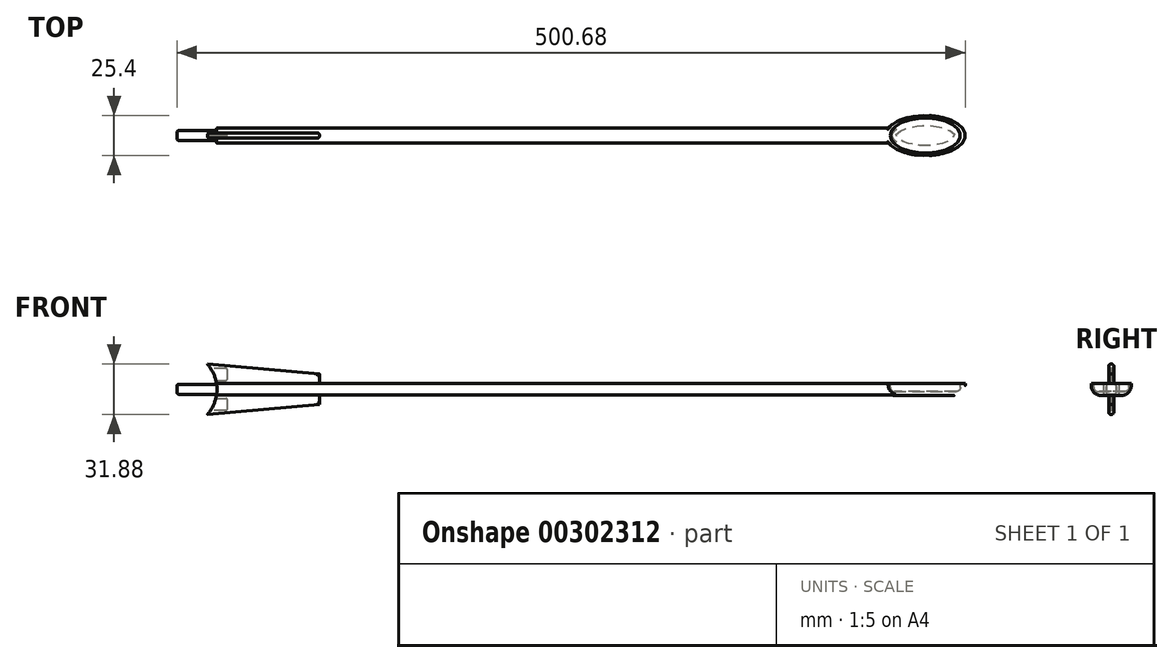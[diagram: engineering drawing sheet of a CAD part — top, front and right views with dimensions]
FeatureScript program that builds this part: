
annotation { "Feature Type Name" : "Feature", "Feature Type Description" : "" }
export const myFeature = defineFeature(function(context is Context, id is Id, definition is map)
    precondition{}
    {
        {
            var Q0;
            Q0=qCreatedBy(makeId("Top.planeOp"),FACE);
            var sketch = newSketch(context, id + "F0", { "sketchPlane" : qUnion([Q0])});
            skLineSegment(sketch, "E0.bottom", {"start": v(-215.55, -4.76) * mm, "end": v(215.55, -4.76) * mm});
            skLineSegment(sketch, "E0.top", {"start": v(-215.55, 4.76) * mm, "end": v(215.55, 4.76) * mm});
            skLineSegment(sketch, "E0.left", {"start": v(-215.55, -4.76) * mm, "end": v(-215.55, 4.76) * mm});
            skLineSegment(sketch, "E0.right", {"start": v(215.55, -4.76) * mm, "end": v(215.55, 4.76) * mm});
            skPoint(sketch, "E0.middle", {"position": v(0, 0) * mm});
            skSolve(sketch);
        }
        {
            var Q0;
            Q0 = qSketchRegion(id + "F0", true);
            extrude(context, id + "F1", {"entities" : qUnion([Q0]), "depth" : 7.24 * mm});
        }
        {
            var Q0;
            Q0=makeQuery(id+"F1.opExtrude","CAP_EDGE",EDGE,{"disambiguationData":[OSD([sQuery(id+"F0.wireOp",EDGE,"E0.bottom")])],"isStart":false});
            var Q1;
            Q1=makeQuery(id+"F1.opExtrude","CAP_EDGE",EDGE,{"disambiguationData":[OSD([sQuery(id+"F0.wireOp",EDGE,"E0.top")])],"isStart":false});
            var Q2;
            Q2=makeQuery(id+"F1.opExtrude","CAP_EDGE",EDGE,{"disambiguationData":[OSD([sQuery(id+"F0.wireOp",EDGE,"E0.bottom")])],"isStart":true});
            var Q3;
            Q3=makeQuery(id+"F1.opExtrude","CAP_EDGE",EDGE,{"disambiguationData":[OSD([sQuery(id+"F0.wireOp",EDGE,"E0.top")])],"isStart":true});
            fillet(context, id + "F2", {"entities" : qUnion([Q0, Q1, Q2, Q3]), "radius" : 1.27 * mm, "tangentPropagation" : true, "allowEdgeOverflow" : false});
        }
        {
            var Q0;
            Q0=makeQuery(id+"F1.opExtrude","CAP_FACE",FACE,{"disambiguationData":[OSD([sQuery(id+"F0.wireOp",EDGE,"E0.bottom"),sQuery(id+"F0.wireOp",EDGE,"E0.top"),sQuery(id+"F0.wireOp",EDGE,"E0.left"),sQuery(id+"F0.wireOp",EDGE,"E0.right")])],"isStart":false});
            var sketch = newSketch(context, id + "F3", { "sketchPlane" : qUnion([Q0])});
            skEllipse(sketch, "E1", {"center": v(234.6, 0) * mm, "majorRadius": 25.4 * mm, "minorRadius": 12.7 * mm, "majorAxis": v(-1, 0)});
            skPoint(sketch, "E1.centerSnap0", {"position": v(215.55, 0) * mm});
            skSolve(sketch);
        }
        {
            var Q0;
            Q0 = qSketchRegion(id + "F3", true);
            extrude(context, id + "F4", {"entities" : qUnion([Q0]), "operationType" : NewBodyOperationType.ADD, "oppositeDirection" : true, "depth" : 7.62 * mm});
        }
        {
            var Q0;
            Q0=makeQuery(id+"F4.opExtrude","CAP_EDGE",EDGE,{"disambiguationData":[OSD([sQuery(id+"F3.wireOp",EDGE,"E1")])],"isStart":false});
            fillet(context, id + "F5", {"entities" : qUnion([Q0]), "radius" : 6.35 * mm, "tangentPropagation" : true, "allowEdgeOverflow" : false});
        }
        {
            var Q0;
            Q0=makeQuery(id+"F4.boolean.opBoolean","MERGE",FACE,{"derivedFrom":[makeQuery(id+"F1.opExtrude","CAP_FACE",FACE,{"disambiguationData":[OSD([sQuery(id+"F0.wireOp",EDGE,"E0.bottom"),sQuery(id+"F0.wireOp",EDGE,"E0.top"),sQuery(id+"F0.wireOp",EDGE,"E0.left"),sQuery(id+"F0.wireOp",EDGE,"E0.right")])],"isStart":false}),makeQuery(id+"F4.opExtrude","CAP_FACE",FACE,{"disambiguationData":[OSD([sQuery(id+"F3.wireOp",EDGE,"E1")])],"isStart":true})]});
            var sketch = newSketch(context, id + "F6", { "sketchPlane" : qUnion([Q0])});
            skEllipse(sketch, "E2", {"center": v(234.6, 0) * mm, "majorRadius": 22.23 * mm, "minorRadius": 11.11 * mm, "majorAxis": v(-1, 0)});
            skSolve(sketch);
        }
        {
            var Q0;
            Q0 = qSketchRegion(id + "F6", true);
            extrude(context, id + "F7", {"entities" : qUnion([Q0]), "operationType" : NewBodyOperationType.REMOVE, "oppositeDirection" : true, "depth" : 5.08 * mm});
        }
        {
            var Q0;
            Q0=makeQuery(id+"F7.boolean.opBoolean","COPY",EDGE,{"derivedFrom":makeQuery(id+"F7.opExtrude","CAP_EDGE",EDGE,{"disambiguationData":[OSD([sQuery(id+"F6.wireOp",EDGE,"E2")])],"isStart":false})});
            fillet(context, id + "F8", {"entities" : qUnion([Q0]), "radius" : 2.54 * mm, "tangentPropagation" : true, "allowEdgeOverflow" : false});
        }
        {
            var Q0;
            Q0=makeQuery(id+"F1.opExtrude","SWEPT_FACE",FACE,{"disambiguationData":[OSD([sQuery(id+"F0.wireOp",EDGE,"E0.bottom")])]});
            var sketch = newSketch(context, id + "F9", { "sketchPlane" : qUnion([Q0])});
            skCircle(sketch, "E3", {"center": v(-239.09, 3.62) * mm, "radius": 23.81 * mm});
            skSolve(sketch);
        }
        {
            var Q0;
            Q0=qCreatedBy(makeId("Front.planeOp"),FACE);
            var sketch = newSketch(context, id + "F10", { "sketchPlane" : qUnion([Q0])});
            skLineSegment(sketch, "E4", {"start": v(-215.55, 7.24) * mm, "end": v(-228.5, 20.18) * mm});
            skLineSegment(sketch, "E5", {"start": v(-228.5, 20.18) * mm, "end": v(-150.2, 13.34) * mm});
            skLineSegment(sketch, "E6", {"start": v(-150.2, 13.34) * mm, "end": v(-150.2, 7.24) * mm});
            skLineSegment(sketch, "E7", {"start": v(-150.2, 7.24) * mm, "end": v(-215.55, 7.24) * mm});
            skLineSegment(sketch, "E8", {"start": v(-150.2, 0) * mm, "end": v(-150.2, -6.1) * mm});
            skLineSegment(sketch, "E9", {"start": v(-150.2, -6.1) * mm, "end": v(-228.5, -12.95) * mm});
            skLineSegment(sketch, "E10", {"start": v(-228.5, -12.95) * mm, "end": v(-215.55, 0) * mm});
            skLineSegment(sketch, "E11", {"start": v(-215.55, 0) * mm, "end": v(-150.2, 0) * mm});
            skSolve(sketch);
        }
        {
            var Q0;
            Q0=makeQuery(id+"F10.imprint","IMPRINT",FACE,{"disambiguationData":[TD([[makeQuery(id+"F10.imprint","IMPRINT",EDGE,{"derivedFrom":sQuery(id+"F10.wireOp",EDGE,"E4")}),-1.0]])]});
            var Q1;
            Q1=makeQuery(id+"F10.imprint","IMPRINT",FACE,{"disambiguationData":[TD([[makeQuery(id+"F10.imprint","IMPRINT",EDGE,{"derivedFrom":sQuery(id+"F10.wireOp",EDGE,"E8")}),-1.0]])]});
            var Q2;
            Q2 = qConstructionFilter(qBodyType(qCreatedBy(id + "F10" ,EDGE), BodyType.WIRE), ConstructionObject.NO);
            extrude(context, id + "F11", {"entities" : qUnion([Q0, Q1]), "operationType" : NewBodyOperationType.ADD, "surfaceEntities" : qUnion([Q2]), "endBound" : BoundingType.SYMMETRIC, "depth" : 3.17 * mm});
        }
        {
            var Q0;
            Q0 = qSketchRegion(id + "F9", true);
            extrude(context, id + "F12", {"entities" : qUnion([Q0]), "operationType" : NewBodyOperationType.REMOVE, "oppositeDirection" : true, "depth" : 25.4 * mm});
        }
        {
            var Q0;
            Q0=makeQuery(id+"F11.opExtrude","CAP_EDGE",EDGE,{"disambiguationData":[OSD([sQuery(id+"F10.wireOp",EDGE,"E5")])],"isStart":false});
            var Q1;
            Q1=makeQuery(id+"F11.opExtrude","CAP_EDGE",EDGE,{"disambiguationData":[OSD([sQuery(id+"F10.wireOp",EDGE,"E5")])],"isStart":true});
            var Q2;
            Q2=makeQuery(id+"F11.opExtrude","CAP_EDGE",EDGE,{"disambiguationData":[OSD([sQuery(id+"F10.wireOp",EDGE,"E7")])],"isStart":false});
            var Q3;
            Q3=makeQuery(id+"F11.opExtrude","SWEPT_EDGE",EDGE,{"disambiguationData":[OSD([sQuery(id+"F10.wireOp",EDGE,"E6"),sQuery(id+"F10.wireOp",EDGE,"E7")])]});
            var Q4;
            Q4=makeQuery(id+"F11.opExtrude","CAP_EDGE",EDGE,{"disambiguationData":[OSD([sQuery(id+"F10.wireOp",EDGE,"E6")])],"isStart":false});
            var Q5;
            Q5=makeQuery(id+"F11.opExtrude","CAP_EDGE",EDGE,{"disambiguationData":[OSD([sQuery(id+"F10.wireOp",EDGE,"E6")])],"isStart":true});
            var Q6;
            Q6=makeQuery(id+"F11.opExtrude","CAP_EDGE",EDGE,{"disambiguationData":[OSD([sQuery(id+"F10.wireOp",EDGE,"E7")])],"isStart":true});
            var Q7;
            Q7=makeQuery(id+"F11.opExtrude","CAP_EDGE",EDGE,{"disambiguationData":[OSD([sQuery(id+"F10.wireOp",EDGE,"E9")])],"isStart":true});
            var Q8;
            Q8=makeQuery(id+"F11.opExtrude","CAP_EDGE",EDGE,{"disambiguationData":[OSD([sQuery(id+"F10.wireOp",EDGE,"E8")])],"isStart":true});
            var Q9;
            Q9=makeQuery(id+"F11.opExtrude","CAP_EDGE",EDGE,{"disambiguationData":[OSD([sQuery(id+"F10.wireOp",EDGE,"E9")])],"isStart":false});
            var Q10;
            Q10=makeQuery(id+"F11.opExtrude","CAP_EDGE",EDGE,{"disambiguationData":[OSD([sQuery(id+"F10.wireOp",EDGE,"E8")])],"isStart":false});
            var Q11;
            Q11=makeQuery(id+"F11.opExtrude","CAP_EDGE",EDGE,{"disambiguationData":[OSD([sQuery(id+"F10.wireOp",EDGE,"E11")])],"isStart":false});
            var Q12;
            Q12=makeQuery(id+"F11.opExtrude","CAP_EDGE",EDGE,{"disambiguationData":[OSD([sQuery(id+"F10.wireOp",EDGE,"E11")])],"isStart":true});
            fillet(context, id + "F13", {"entities" : qUnion([Q0, Q1, Q2, Q3, Q4, Q5, Q6, Q7, Q8, Q9, Q10, Q11, Q12]), "radius" : 1.27 * mm, "tangentPropagation" : true, "allowEdgeOverflow" : false});
        }
        {
            var Q0;
            Q0=qCreatedBy(makeId("Right.planeOp"),FACE);
            var sketch = newSketch(context, id + "F14", { "sketchPlane" : qUnion([Q0])});
            skLineSegment(sketch, "E12.bottom", {"start": v(-3.17, 6.8) * mm, "end": v(3.18, 6.8) * mm});
            skLineSegment(sketch, "E12.top", {"start": v(-3.18, 0.44) * mm, "end": v(3.18, 0.44) * mm});
            skLineSegment(sketch, "E12.left", {"start": v(-3.17, 6.8) * mm, "end": v(-3.18, 0.44) * mm});
            skLineSegment(sketch, "E12.right", {"start": v(3.18, 6.8) * mm, "end": v(3.18, 0.44) * mm});
            skPoint(sketch, "E12.middle", {"position": v(0, 3.62) * mm});
            skSolve(sketch);
        }
        {
            var Q0;
            Q0 = qSketchRegion(id + "F14", true);
            extrude(context, id + "F15", {"entities" : qUnion([Q0]), "operationType" : NewBodyOperationType.ADD, "oppositeDirection" : true, "depth" : 241.3 * mm});
        }
        {
            var Q0;
            Q0=makeQuery(id+"F15.opExtrude","CAP_FACE",FACE,{"disambiguationData":[OSD([sQuery(id+"F14.wireOp",EDGE,"E12.bottom"),sQuery(id+"F14.wireOp",EDGE,"E12.top"),sQuery(id+"F14.wireOp",EDGE,"E12.left"),sQuery(id+"F14.wireOp",EDGE,"E12.right")])],"isStart":false});
            extrude(context, id + "F16", {"entities" : qUnion([Q0]), "operationType" : NewBodyOperationType.REMOVE, "oppositeDirection" : true, "depth" : 0.62 * mm});
        }
        {
            var Q0;
            Q0=makeQuery(id+"F15.opExtrude","SWEPT_EDGE",EDGE,{"disambiguationData":[OSD([sQuery(id+"F14.wireOp",EDGE,"E12.bottom"),sQuery(id+"F14.wireOp",EDGE,"E12.right")])]});
            var Q1;
            Q1=makeQuery(id+"F15.opExtrude","SWEPT_EDGE",EDGE,{"disambiguationData":[OSD([sQuery(id+"F14.wireOp",EDGE,"E12.top"),sQuery(id+"F14.wireOp",EDGE,"E12.right")])]});
            var Q2;
            Q2=makeQuery(id+"F15.opExtrude","SWEPT_EDGE",EDGE,{"disambiguationData":[OSD([sQuery(id+"F14.wireOp",EDGE,"E12.bottom"),sQuery(id+"F14.wireOp",EDGE,"E12.left")])]});
            var Q3;
            Q3=makeQuery(id+"F15.opExtrude","SWEPT_EDGE",EDGE,{"disambiguationData":[OSD([sQuery(id+"F14.wireOp",EDGE,"E12.top"),sQuery(id+"F14.wireOp",EDGE,"E12.left")])]});
            var Q4;
            Q4=makeQuery(id+"F16.boolean.opBoolean","COPY",FACE,{"derivedFrom":makeQuery(id+"F16.opExtrude","CAP_FACE",FACE,{"disambiguationData":[OSD([sQuery(id+"F14.wireOp",EDGE,"E12.bottom"),sQuery(id+"F14.wireOp",EDGE,"E12.top"),sQuery(id+"F14.wireOp",EDGE,"E12.left"),sQuery(id+"F14.wireOp",EDGE,"E12.right")])],"isStart":false})});
            fillet(context, id + "F17", {"entities" : qUnion([Q0, Q1, Q2, Q3, Q4]), "radius" : 1.27 * mm, "tangentPropagation" : true, "allowEdgeOverflow" : false});
        }
        {
            var Q0;
            Q0=makeQuery(id+"F16.boolean.opBoolean","COPY",FACE,{"derivedFrom":makeQuery(id+"F16.opExtrude","CAP_FACE",FACE,{"disambiguationData":[OSD([sQuery(id+"F14.wireOp",EDGE,"E12.bottom"),sQuery(id+"F14.wireOp",EDGE,"E12.top"),sQuery(id+"F14.wireOp",EDGE,"E12.left"),sQuery(id+"F14.wireOp",EDGE,"E12.right")])],"isStart":false})});
            var sketch = newSketch(context, id + "F18", { "sketchPlane" : qUnion([Q0])});
            skLineSegment(sketch, "E13.bottom", {"start": v(0.63, 9.33) * mm, "end": v(-0.64, 9.33) * mm});
            skLineSegment(sketch, "E13.top", {"start": v(0.63, 16.95) * mm, "end": v(-0.64, 16.95) * mm});
            skLineSegment(sketch, "E13.left", {"start": v(0.63, 9.33) * mm, "end": v(0.63, 16.95) * mm});
            skLineSegment(sketch, "E13.right", {"start": v(-0.64, 9.33) * mm, "end": v(-0.64, 16.95) * mm});
            skPoint(sketch, "E13.middle", {"position": v(0, 13.14) * mm});
            skLineSegment(sketch, "E14.bottom", {"start": v(0.63, -2.1) * mm, "end": v(-0.64, -2.1) * mm});
            skLineSegment(sketch, "E14.top", {"start": v(0.64, -9.72) * mm, "end": v(-0.63, -9.72) * mm});
            skLineSegment(sketch, "E14.left", {"start": v(0.63, -2.1) * mm, "end": v(0.64, -9.72) * mm});
            skLineSegment(sketch, "E14.right", {"start": v(-0.64, -2.1) * mm, "end": v(-0.63, -9.72) * mm});
            skPoint(sketch, "E14.middle", {"position": v(0, -5.9) * mm});
            skSolve(sketch);
        }
        {
            var Q0;
            Q0 = qSketchRegion(id + "F18", true);
            extrude(context, id + "F19", {"entities" : qUnion([Q0]), "operationType" : NewBodyOperationType.REMOVE, "oppositeDirection" : true, "depth" : 31.75 * mm});
        }
        {
            var Q0;
            Q0=makeQuery(id+"F19.boolean.opBoolean","COPY",FACE,{"derivedFrom":makeQuery(id+"F19.opExtrude","CAP_FACE",FACE,{"disambiguationData":[OSD([sQuery(id+"F18.wireOp",EDGE,"E13.bottom"),sQuery(id+"F18.wireOp",EDGE,"E13.top"),sQuery(id+"F18.wireOp",EDGE,"E13.left"),sQuery(id+"F18.wireOp",EDGE,"E13.right")])],"isStart":false})});
            var Q1;
            Q1=makeQuery(id+"F19.boolean.opBoolean","COPY",FACE,{"derivedFrom":makeQuery(id+"F19.opExtrude","CAP_FACE",FACE,{"disambiguationData":[OSD([sQuery(id+"F18.wireOp",EDGE,"E14.bottom"),sQuery(id+"F18.wireOp",EDGE,"E14.top"),sQuery(id+"F18.wireOp",EDGE,"E14.left"),sQuery(id+"F18.wireOp",EDGE,"E14.right")])],"isStart":false})});
            var Q2;
            Q2=makeQuery(id+"F19.boolean.opBoolean","COPY",EDGE,{"derivedFrom":makeQuery(id+"F19.opExtrude","SWEPT_EDGE",EDGE,{"disambiguationData":[OSD([sQuery(id+"F18.wireOp",EDGE,"E13.bottom"),sQuery(id+"F18.wireOp",EDGE,"E13.left")])]})});
            var Q3;
            Q3=makeQuery(id+"F19.boolean.opBoolean","COPY",EDGE,{"derivedFrom":makeQuery(id+"F19.opExtrude","SWEPT_EDGE",EDGE,{"disambiguationData":[OSD([sQuery(id+"F18.wireOp",EDGE,"E14.top"),sQuery(id+"F18.wireOp",EDGE,"E14.left")])]})});
            var Q4;
            Q4=makeQuery(id+"F19.boolean.opBoolean","COPY",EDGE,{"derivedFrom":makeQuery(id+"F19.opExtrude","SWEPT_EDGE",EDGE,{"disambiguationData":[OSD([sQuery(id+"F18.wireOp",EDGE,"E13.bottom"),sQuery(id+"F18.wireOp",EDGE,"E13.right")])]})});
            var Q5;
            Q5=makeQuery(id+"F19.boolean.opBoolean","COPY",EDGE,{"derivedFrom":makeQuery(id+"F19.opExtrude","SWEPT_EDGE",EDGE,{"disambiguationData":[OSD([sQuery(id+"F18.wireOp",EDGE,"E14.top"),sQuery(id+"F18.wireOp",EDGE,"E14.right")])]})});
            var Q6;
            Q6=makeQuery(id+"F19.boolean.opBoolean","COPY",EDGE,{"derivedFrom":makeQuery(id+"F19.opExtrude","SWEPT_EDGE",EDGE,{"disambiguationData":[OSD([sQuery(id+"F18.wireOp",EDGE,"E13.top"),sQuery(id+"F18.wireOp",EDGE,"E13.right")])]})});
            var Q7;
            Q7=makeQuery(id+"F19.boolean.opBoolean","COPY",EDGE,{"derivedFrom":makeQuery(id+"F19.opExtrude","SWEPT_EDGE",EDGE,{"disambiguationData":[OSD([sQuery(id+"F18.wireOp",EDGE,"E14.bottom"),sQuery(id+"F18.wireOp",EDGE,"E14.right")])]})});
            var Q8;
            Q8=makeQuery(id+"F19.boolean.opBoolean","COPY",EDGE,{"derivedFrom":makeQuery(id+"F19.opExtrude","SWEPT_EDGE",EDGE,{"disambiguationData":[OSD([sQuery(id+"F18.wireOp",EDGE,"E13.top"),sQuery(id+"F18.wireOp",EDGE,"E13.left")])]})});
            var Q9;
            Q9=makeQuery(id+"F19.boolean.opBoolean","COPY",EDGE,{"derivedFrom":makeQuery(id+"F19.opExtrude","SWEPT_EDGE",EDGE,{"disambiguationData":[OSD([sQuery(id+"F18.wireOp",EDGE,"E14.bottom"),sQuery(id+"F18.wireOp",EDGE,"E14.left")])]})});
            fillet(context, id + "F20", {"entities" : qUnion([Q0, Q1, Q2, Q3, Q4, Q5, Q6, Q7, Q8, Q9]), "radius" : 0.64 * mm, "tangentPropagation" : true, "allowEdgeOverflow" : false});
        }
    });
